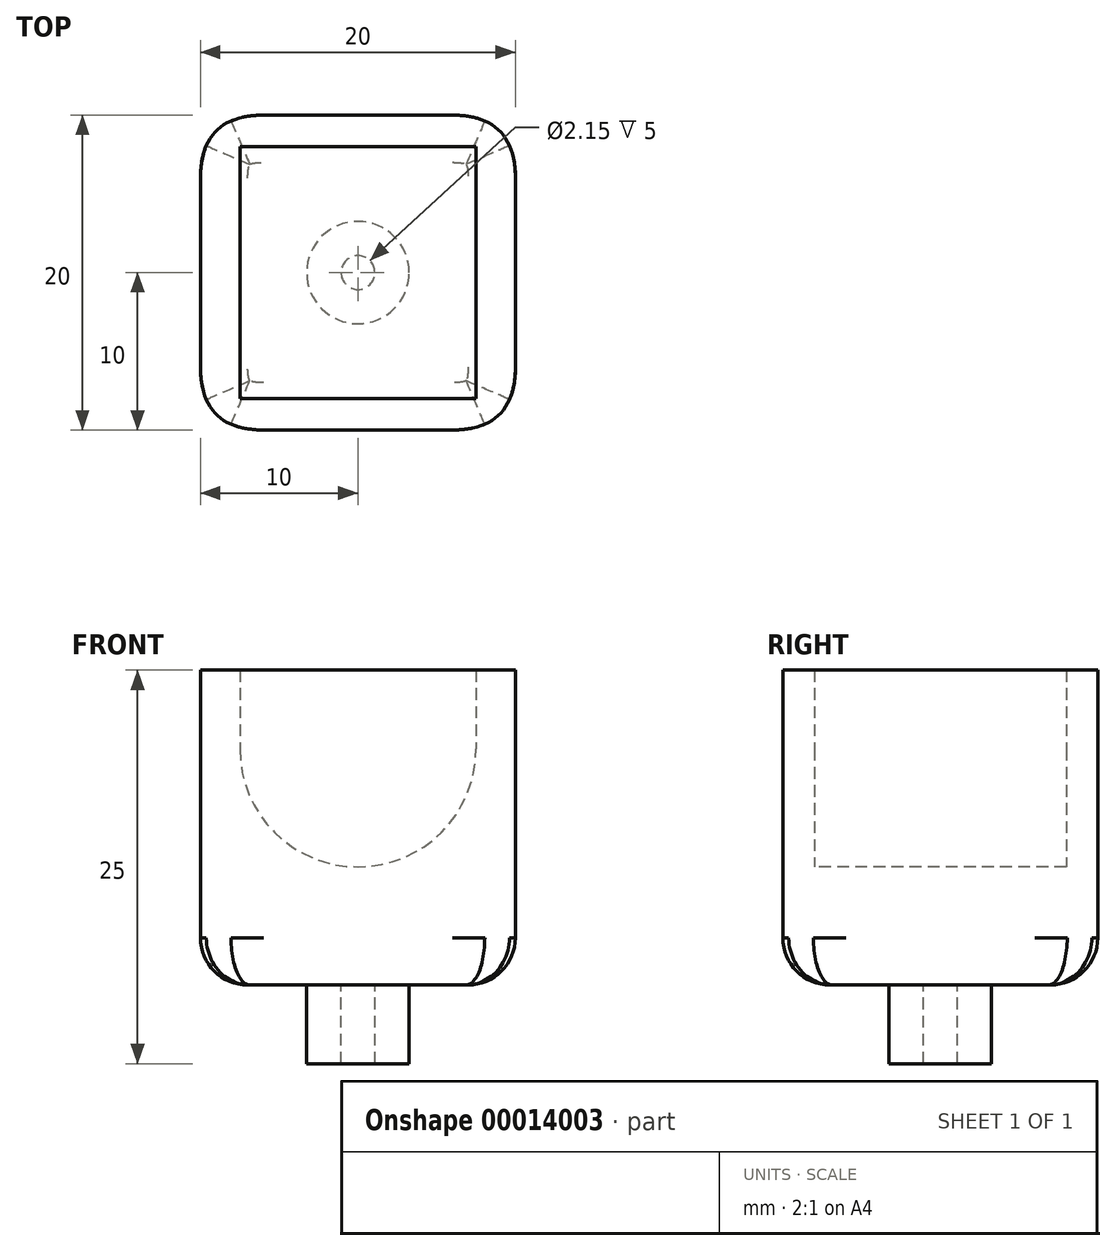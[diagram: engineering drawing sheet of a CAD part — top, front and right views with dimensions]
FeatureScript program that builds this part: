
annotation { "Feature Type Name" : "Feature", "Feature Type Description" : "" }
export const myFeature = defineFeature(function(context is Context, id is Id, definition is map)
    precondition{}
    {
        {
            var Q0;
            Q0=qCreatedBy(makeId("Top.planeOp"),FACE);
            var sketch = newSketch(context, id + "F0", { "sketchPlane" : qUnion([Q0])});
            skLineSegment(sketch, "E0.rect.bottom", {"start": v(-10, -10) * mm, "end": v(10, -10) * mm});
            skLineSegment(sketch, "E0.rect.top", {"start": v(-10, 10) * mm, "end": v(10, 10) * mm});
            skLineSegment(sketch, "E0.rect.left", {"start": v(-10, -10) * mm, "end": v(-10, 10) * mm});
            skLineSegment(sketch, "E0.rect.right", {"start": v(10, -10) * mm, "end": v(10, 10) * mm});
            skPoint(sketch, "E0.rect.middle", {"position": v(0, 0) * mm});
            skLineSegment(sketch, "E1.0", {"start": v(-7.5, 7.5) * mm, "end": v(7.5, 7.5) * mm});
            skLineSegment(sketch, "E1.1", {"start": v(-7.5, -7.5) * mm, "end": v(-7.5, 7.5) * mm});
            skLineSegment(sketch, "E1.2", {"start": v(-7.5, -7.5) * mm, "end": v(7.5, -7.5) * mm});
            skLineSegment(sketch, "E1.3", {"start": v(7.5, -7.5) * mm, "end": v(7.5, 7.5) * mm});
            skCircle(sketch, "E2", {"center": v(0, 0) * mm, "radius": 3.25 * mm});
            skCircle(sketch, "E3", {"center": v(0, 0) * mm, "radius": 1.07 * mm});
            skSolve(sketch);
        }
        {
            var Q0;
            Q0=makeQuery(id+"F0.imprint","IMPRINT",FACE,{"disambiguationData":[TD([[makeQuery(id+"F0.imprint","IMPRINT",EDGE,{"derivedFrom":sQuery(id+"F0.wireOp",EDGE,"E0.rect.bottom")}),1.0]])]});
            var Q1;
            Q1=makeQuery(id+"F0.imprint","IMPRINT",FACE,{"disambiguationData":[TD([[makeQuery(id+"F0.imprint","IMPRINT",EDGE,{"derivedFrom":sQuery(id+"F0.wireOp",EDGE,"E1.0")}),-1.0]])]});
            var Q2;
            Q2=makeQuery(id+"F0.imprint","IMPRINT",FACE,{"disambiguationData":[TD([[makeQuery(id+"F0.imprint","IMPRINT",EDGE,{"derivedFrom":sQuery(id+"F0.wireOp",EDGE,"E2")}),1.0]])]});
            var Q3;
            Q3=makeQuery(id+"F0.imprint","IMPRINT",FACE,{"disambiguationData":[TD([[makeQuery(id+"F0.imprint","IMPRINT",EDGE,{"derivedFrom":sQuery(id+"F0.wireOp",EDGE,"E3")}),1.0]])]});
            extrude(context, id + "F1", {"entities" : qUnion([Q0, Q1, Q2, Q3]), "depth" : 15 * mm});
        }
        {
            var Q0;
            Q0=makeQuery(id+"F1.opExtrude","SWEPT_FACE",FACE,{"disambiguationData":[OSD([sQuery(id+"F0.wireOp",EDGE,"E0.rect.bottom")])]});
            var sketch = newSketch(context, id + "F2", { "sketchPlane" : qUnion([Q0])});
            skLineSegment(sketch, "E4", {"start": v(0, 15) * mm, "end": v(0, 7.5) * mm, "construction": true});
            skArc(sketch, "E5", {"start": v(-7.5, 15) * mm, "mid": v(0, 7.5) * mm, "end": v(7.5, 15) * mm});
            skLineSegment(sketch, "E6", {"start": v(-10, 15) * mm, "end": v(10, 15) * mm, "construction": true});
            skLineSegment(sketch, "E7", {"start": v(-7.5, 15) * mm, "end": v(7.5, 15) * mm});
            skSolve(sketch);
        }
        {
            var Q0;
            Q0=makeQuery(id+"F2.imprint","IMPRINT",FACE,{"disambiguationData":[TD([[makeQuery(id+"F2.imprint","IMPRINT",EDGE,{"derivedFrom":sQuery(id+"F2.wireOp",EDGE,"E5")}),1.0]])]});
            extrude(context, id + "F3", {"entities" : qUnion([Q0]), "operationType" : NewBodyOperationType.REMOVE, "oppositeDirection" : true, "depth" : 18 * mm, "hasSecondDirection" : true, "secondDirectionOppositeDirection" : true, "secondDirectionDepth" : 2 * mm});
        }
        {
            var Q0;
            Q0=makeQuery(id+"F0.imprint","IMPRINT",FACE,{"disambiguationData":[TD([[makeQuery(id+"F0.imprint","IMPRINT",EDGE,{"derivedFrom":sQuery(id+"F0.wireOp",EDGE,"E2")}),1.0]])]});
            extrude(context, id + "F4", {"entities" : qUnion([Q0]), "operationType" : NewBodyOperationType.ADD, "oppositeDirection" : true, "depth" : 5 * mm});
        }
        {
            var Q0;
            Q0=makeQuery(id+"F1.opExtrude","SWEPT_EDGE",EDGE,{"disambiguationData":[OSD([sQuery(id+"F0.wireOp",EDGE,"E0.rect.bottom"),sQuery(id+"F0.wireOp",EDGE,"E0.rect.right")])]});
            var Q1;
            Q1=makeQuery(id+"F1.opExtrude","SWEPT_EDGE",EDGE,{"disambiguationData":[OSD([sQuery(id+"F0.wireOp",EDGE,"E0.rect.bottom"),sQuery(id+"F0.wireOp",EDGE,"E0.rect.left")])]});
            var Q2;
            Q2=makeQuery(id+"F1.opExtrude","SWEPT_EDGE",EDGE,{"disambiguationData":[OSD([sQuery(id+"F0.wireOp",EDGE,"E0.rect.top"),sQuery(id+"F0.wireOp",EDGE,"E0.rect.right")])]});
            var Q3;
            Q3=makeQuery(id+"F1.opExtrude","SWEPT_EDGE",EDGE,{"disambiguationData":[OSD([sQuery(id+"F0.wireOp",EDGE,"E0.rect.top"),sQuery(id+"F0.wireOp",EDGE,"E0.rect.left")])]});
            fillet(context, id + "F5", {"entities" : qUnion([Q0, Q1, Q2, Q3]), "radius" : 4 * mm, "tangentPropagation" : true, "rho" : 0.5, "crossSection" : FilletCrossSection.CONIC, "allowEdgeOverflow" : false});
        }
        {
            var Q0;
            {var subQ0=sQuery(id+"F0.wireOp",EDGE,"E0.rect.top");var subQ1=sQuery(id+"F0.wireOp",EDGE,"E0.rect.left");var subQ2=sQuery(id+"F0.wireOp",EDGE,"E0.rect.bottom");var subQ3=sQuery(id+"F0.wireOp",EDGE,"E0.rect.right");Q0=makeQuery(id+"F5.opFillet","BLEND_EDGE",EDGE,{"blendedFrom":[makeQuery(id+"F1.opExtrude","SWEPT_EDGE",EDGE,{"disambiguationData":[OSD([subQ0,subQ1])]}),makeQuery(id+"F4.boolean.opBoolean","SPLIT",FACE,{"disambiguationData":[TD([makeQuery(id+"F1.opExtrude","SWEPT_FACE",FACE,{"disambiguationData":[OSD([subQ2])]})])],"derivedFrom":makeQuery(id+"F1.opExtrude","CAP_FACE",FACE,{"disambiguationData":[OSD([subQ2,subQ0,subQ1,subQ3])],"isStart":true})})],"blendedInto":[makeQuery(id+"F4.boolean.opBoolean","SPLIT",FACE,{"disambiguationData":[TD([makeQuery(id+"F1.opExtrude","SWEPT_FACE",FACE,{"disambiguationData":[OSD([subQ2])]})])],"derivedFrom":makeQuery(id+"F1.opExtrude","CAP_FACE",FACE,{"disambiguationData":[OSD([subQ2,subQ0,subQ1,subQ3])],"isStart":true})})]});}
            var Q1;
            Q1=makeQuery(id+"F1.opExtrude","CAP_EDGE",EDGE,{"disambiguationData":[OSD([sQuery(id+"F0.wireOp",EDGE,"E0.rect.left")])],"isStart":true});
            var Q2;
            {var subQ0=sQuery(id+"F0.wireOp",EDGE,"E0.rect.bottom");var subQ1=sQuery(id+"F0.wireOp",EDGE,"E0.rect.left");var subQ2=sQuery(id+"F0.wireOp",EDGE,"E0.rect.top");var subQ3=sQuery(id+"F0.wireOp",EDGE,"E0.rect.right");Q2=makeQuery(id+"F5.opFillet","BLEND_EDGE",EDGE,{"blendedFrom":[makeQuery(id+"F1.opExtrude","SWEPT_EDGE",EDGE,{"disambiguationData":[OSD([subQ0,subQ1])]}),makeQuery(id+"F4.boolean.opBoolean","SPLIT",FACE,{"disambiguationData":[TD([makeQuery(id+"F1.opExtrude","SWEPT_FACE",FACE,{"disambiguationData":[OSD([subQ0])]})])],"derivedFrom":makeQuery(id+"F1.opExtrude","CAP_FACE",FACE,{"disambiguationData":[OSD([subQ0,subQ2,subQ1,subQ3])],"isStart":true})})],"blendedInto":[makeQuery(id+"F4.boolean.opBoolean","SPLIT",FACE,{"disambiguationData":[TD([makeQuery(id+"F1.opExtrude","SWEPT_FACE",FACE,{"disambiguationData":[OSD([subQ0])]})])],"derivedFrom":makeQuery(id+"F1.opExtrude","CAP_FACE",FACE,{"disambiguationData":[OSD([subQ0,subQ2,subQ1,subQ3])],"isStart":true})})]});}
            var Q3;
            Q3=makeQuery(id+"F1.opExtrude","CAP_EDGE",EDGE,{"disambiguationData":[OSD([sQuery(id+"F0.wireOp",EDGE,"E0.rect.bottom")])],"isStart":true});
            var Q4;
            {var subQ0=sQuery(id+"F0.wireOp",EDGE,"E0.rect.bottom");var subQ1=sQuery(id+"F0.wireOp",EDGE,"E0.rect.right");var subQ2=sQuery(id+"F0.wireOp",EDGE,"E0.rect.top");var subQ3=sQuery(id+"F0.wireOp",EDGE,"E0.rect.left");Q4=makeQuery(id+"F5.opFillet","BLEND_EDGE",EDGE,{"blendedFrom":[makeQuery(id+"F1.opExtrude","SWEPT_EDGE",EDGE,{"disambiguationData":[OSD([subQ0,subQ1])]}),makeQuery(id+"F4.boolean.opBoolean","SPLIT",FACE,{"disambiguationData":[TD([makeQuery(id+"F1.opExtrude","SWEPT_FACE",FACE,{"disambiguationData":[OSD([subQ0])]})])],"derivedFrom":makeQuery(id+"F1.opExtrude","CAP_FACE",FACE,{"disambiguationData":[OSD([subQ0,subQ2,subQ3,subQ1])],"isStart":true})})],"blendedInto":[makeQuery(id+"F4.boolean.opBoolean","SPLIT",FACE,{"disambiguationData":[TD([makeQuery(id+"F1.opExtrude","SWEPT_FACE",FACE,{"disambiguationData":[OSD([subQ0])]})])],"derivedFrom":makeQuery(id+"F1.opExtrude","CAP_FACE",FACE,{"disambiguationData":[OSD([subQ0,subQ2,subQ3,subQ1])],"isStart":true})})]});}
            var Q5;
            Q5=makeQuery(id+"F1.opExtrude","CAP_EDGE",EDGE,{"disambiguationData":[OSD([sQuery(id+"F0.wireOp",EDGE,"E0.rect.right")])],"isStart":true});
            var Q6;
            {var subQ0=sQuery(id+"F0.wireOp",EDGE,"E0.rect.top");var subQ1=sQuery(id+"F0.wireOp",EDGE,"E0.rect.right");var subQ2=sQuery(id+"F0.wireOp",EDGE,"E0.rect.bottom");var subQ3=sQuery(id+"F0.wireOp",EDGE,"E0.rect.left");Q6=makeQuery(id+"F5.opFillet","BLEND_EDGE",EDGE,{"blendedFrom":[makeQuery(id+"F1.opExtrude","SWEPT_EDGE",EDGE,{"disambiguationData":[OSD([subQ0,subQ1])]}),makeQuery(id+"F4.boolean.opBoolean","SPLIT",FACE,{"disambiguationData":[TD([makeQuery(id+"F1.opExtrude","SWEPT_FACE",FACE,{"disambiguationData":[OSD([subQ2])]})])],"derivedFrom":makeQuery(id+"F1.opExtrude","CAP_FACE",FACE,{"disambiguationData":[OSD([subQ2,subQ0,subQ3,subQ1])],"isStart":true})})],"blendedInto":[makeQuery(id+"F4.boolean.opBoolean","SPLIT",FACE,{"disambiguationData":[TD([makeQuery(id+"F1.opExtrude","SWEPT_FACE",FACE,{"disambiguationData":[OSD([subQ2])]})])],"derivedFrom":makeQuery(id+"F1.opExtrude","CAP_FACE",FACE,{"disambiguationData":[OSD([subQ2,subQ0,subQ3,subQ1])],"isStart":true})})]});}
            var Q7;
            Q7=makeQuery(id+"F1.opExtrude","CAP_EDGE",EDGE,{"disambiguationData":[OSD([sQuery(id+"F0.wireOp",EDGE,"E0.rect.top")])],"isStart":true});
            fillet(context, id + "F6", {"entities" : qUnion([Q0, Q1, Q2, Q3, Q4, Q5, Q6, Q7]), "radius" : 3 * mm, "tangentPropagation" : true, "allowEdgeOverflow" : false});
        }
        {
            var Q0;
            Q0=makeQuery(id+"F1.opExtrude","CAP_FACE",FACE,{"disambiguationData":[OSD([sQuery(id+"F0.wireOp",EDGE,"E0.rect.bottom"),sQuery(id+"F0.wireOp",EDGE,"E0.rect.top"),sQuery(id+"F0.wireOp",EDGE,"E0.rect.left"),sQuery(id+"F0.wireOp",EDGE,"E0.rect.right")])],"isStart":false});
            extrude(context, id + "F7", {"entities" : qUnion([Q0]), "operationType" : NewBodyOperationType.ADD, "depth" : 5 * mm});
        }
    });
